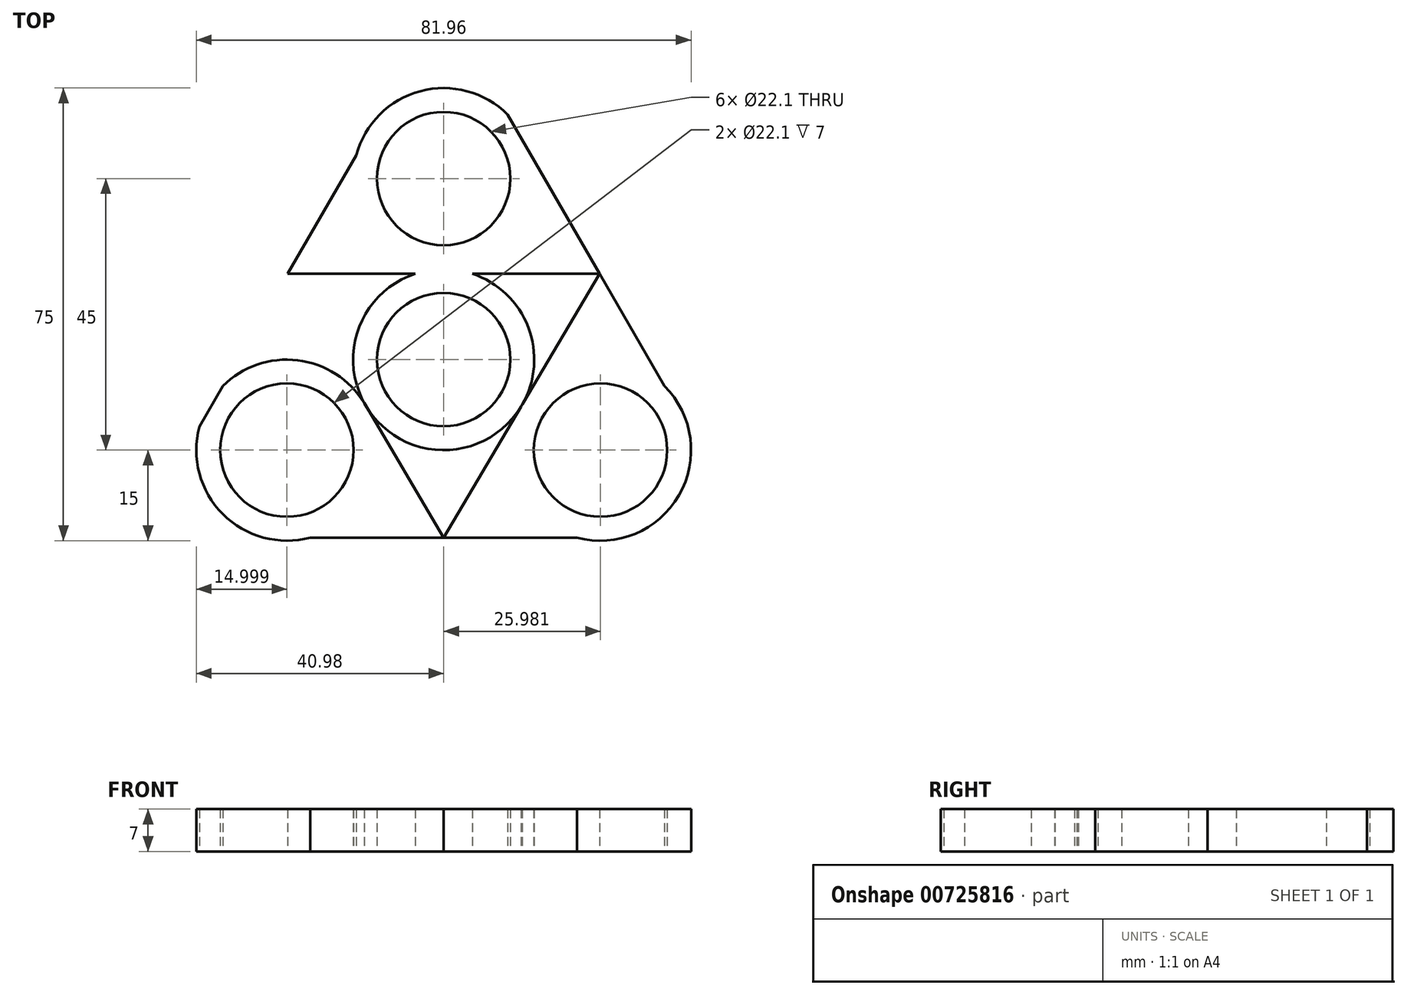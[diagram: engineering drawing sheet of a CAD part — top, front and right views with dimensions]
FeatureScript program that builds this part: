
annotation { "Feature Type Name" : "Feature", "Feature Type Description" : "" }
export const myFeature = defineFeature(function(context is Context, id is Id, definition is map)
    precondition{}
    {
        {
            var Q0;
            Q0=qCreatedBy(makeId("Top.planeOp"),FACE);
            var sketch = newSketch(context, id + "F0", { "sketchPlane" : qUnion([Q0])});
            skCircle(sketch, "E0", {"center": v(0, 0) * mm, "radius": 11.05 * mm});
            skCircle(sketch, "E1", {"center": v(0, 0) * mm, "radius": 15 * mm});
            skCircle(sketch, "E2", {"center": v(0, 30) * mm, "radius": 11.05 * mm});
            skCircle(sketch, "E3", {"center": v(0, 30) * mm, "radius": 15 * mm});
            skCircle(sketch, "E4", {"center": v(-25.98, -15) * mm, "radius": 11.05 * mm});
            skCircle(sketch, "E5", {"center": v(25.98, -15) * mm, "radius": 11.05 * mm});
            skCircle(sketch, "E6", {"center": v(-25.98, -15) * mm, "radius": 15 * mm});
            skCircle(sketch, "E7", {"center": v(25.98, -15) * mm, "radius": 15 * mm});
            skLineSegment(sketch, "E8", {"start": v(0, 30) * mm, "end": v(0, 0) * mm, "construction": true});
            skLineSegment(sketch, "E9", {"start": v(-25.98, -15) * mm, "end": v(0, 0) * mm, "construction": true});
            skLineSegment(sketch, "E10", {"start": v(25.98, -15) * mm, "end": v(0, 0) * mm, "construction": true});
            skLineSegment(sketch, "E11", {"start": v(-25.98, -15) * mm, "end": v(-33.48, -2) * mm, "construction": true});
            skLineSegment(sketch, "E12", {"start": v(0, 30) * mm, "end": v(-15, 30) * mm, "construction": true});
            skLineSegment(sketch, "E13", {"start": v(0, 30) * mm, "end": v(15, 30) * mm, "construction": true});
            skLineSegment(sketch, "E14", {"start": v(25.98, -15) * mm, "end": v(33.48, -2) * mm, "construction": true});
            skLineSegment(sketch, "E15", {"start": v(33.48, -2) * mm, "end": v(18.48, -28) * mm, "construction": true});
            skLineSegment(sketch, "E16", {"start": v(0, 30) * mm, "end": v(-10.6, 40.6) * mm, "construction": true});
            skLineSegment(sketch, "E17", {"start": v(0, 30) * mm, "end": v(10.6, 40.6) * mm, "construction": true});
            skLineSegment(sketch, "E18", {"start": v(-25.98, -15) * mm, "end": v(-40.47, -11.12) * mm, "construction": true});
            skLineSegment(sketch, "E19", {"start": v(-25.98, -15) * mm, "end": v(-18.48, -28) * mm, "construction": true});
            skLineSegment(sketch, "E20", {"start": v(-25.98, -15) * mm, "end": v(-29.86, -29.49) * mm, "construction": true});
            skLineSegment(sketch, "E21", {"start": v(25.98, -15) * mm, "end": v(29.86, -29.49) * mm, "construction": true});
            skLineSegment(sketch, "E22", {"start": v(25.98, -15) * mm, "end": v(40.47, -11.12) * mm, "construction": true});
            skLineSegment(sketch, "E23", {"start": v(-40.47, -11.12) * mm, "end": v(-10.6, 40.6) * mm});
            skLineSegment(sketch, "E24", {"start": v(-29.86, -29.49) * mm, "end": v(29.86, -29.49) * mm});
            skLineSegment(sketch, "E25", {"start": v(10.6, 40.6) * mm, "end": v(40.47, -11.12) * mm});
            skLineSegment(sketch, "E26", {"start": v(-25.83, 14.24) * mm, "end": v(0, -29.49) * mm});
            skLineSegment(sketch, "E27", {"start": v(0, -29.49) * mm, "end": v(25.83, 14.24) * mm});
            skLineSegment(sketch, "E28", {"start": v(-25.83, 14.24) * mm, "end": v(25.83, 14.24) * mm, "construction": true});
            skLineSegment(sketch, "E29", {"start": v(-25.83, 14.24) * mm, "end": v(25.83, 14.24) * mm});
            skSolve(sketch);
        }
        {
            var Q0;
            {var subQ0=sQuery(id+"F0.wireOp",EDGE,"E25");var subQ1=sQuery(id+"F0.wireOp",EDGE,"E3");var subQ2=makeQuery(id+"F0.imprint","INTERSECT",VERTEX,{"disambiguationData":[OD(0.0)],"derivedFrom":[subQ1,subQ0]});Q0=makeQuery(id+"F0.imprint","IMPRINT",FACE,{"disambiguationData":[TD([[makeQuery(id+"F0.imprint","IMPRINT",EDGE,{"disambiguationData":[TD([[subQ2,1.0]])],"derivedFrom":subQ1}),1.0]])]});}
            var Q1;
            {var subQ0=sQuery(id+"F0.wireOp",EDGE,"E23");var subQ1=sQuery(id+"F0.wireOp",EDGE,"E3");var subQ2=makeQuery(id+"F0.imprint","INTERSECT",VERTEX,{"disambiguationData":[OD(0.0)],"derivedFrom":[subQ1,subQ0]});Q1=makeQuery(id+"F0.imprint","IMPRINT",FACE,{"disambiguationData":[TD([[makeQuery(id+"F0.imprint","IMPRINT",EDGE,{"disambiguationData":[TD([[subQ2,-1.0]])],"derivedFrom":subQ1}),1.0]])]});}
            var Q2;
            {var subQ0=sQuery(id+"F0.wireOp",EDGE,"E23");var subQ1=sQuery(id+"F0.wireOp",EDGE,"E6");var subQ2=makeQuery(id+"F0.imprint","INTERSECT",VERTEX,{"disambiguationData":[OD(0.0)],"derivedFrom":[subQ1,subQ0]});Q2=makeQuery(id+"F0.imprint","IMPRINT",FACE,{"disambiguationData":[TD([[makeQuery(id+"F0.imprint","IMPRINT",EDGE,{"disambiguationData":[TD([[subQ2,1.0]])],"derivedFrom":subQ1}),1.0]])]});}
            var Q3;
            {var subQ0=sQuery(id+"F0.wireOp",EDGE,"E24");var subQ1=sQuery(id+"F0.wireOp",EDGE,"E6");var subQ2=makeQuery(id+"F0.imprint","INTERSECT",VERTEX,{"disambiguationData":[OD(0.0)],"derivedFrom":[subQ1,subQ0]});Q3=makeQuery(id+"F0.imprint","IMPRINT",FACE,{"disambiguationData":[TD([[makeQuery(id+"F0.imprint","IMPRINT",EDGE,{"disambiguationData":[TD([[subQ2,-1.0]])],"derivedFrom":subQ1}),1.0]])]});}
            var Q4;
            {var subQ0=sQuery(id+"F0.wireOp",EDGE,"E25");var subQ1=sQuery(id+"F0.wireOp",EDGE,"E7");var subQ2=makeQuery(id+"F0.imprint","INTERSECT",VERTEX,{"disambiguationData":[OD(0.0)],"derivedFrom":[subQ1,subQ0]});Q4=makeQuery(id+"F0.imprint","IMPRINT",FACE,{"disambiguationData":[TD([[makeQuery(id+"F0.imprint","IMPRINT",EDGE,{"disambiguationData":[TD([[subQ2,-1.0]])],"derivedFrom":subQ1}),1.0]])]});}
            var Q5;
            {var subQ0=sQuery(id+"F0.wireOp",EDGE,"E24");var subQ1=sQuery(id+"F0.wireOp",EDGE,"E7");var subQ2=makeQuery(id+"F0.imprint","INTERSECT",VERTEX,{"disambiguationData":[OD(0.0)],"derivedFrom":[subQ1,subQ0]});Q5=makeQuery(id+"F0.imprint","IMPRINT",FACE,{"disambiguationData":[TD([[makeQuery(id+"F0.imprint","IMPRINT",EDGE,{"disambiguationData":[TD([[subQ2,1.0]])],"derivedFrom":subQ1}),1.0]])]});}
            var Q6;
            {var subQ0=sQuery(id+"F0.wireOp",EDGE,"E23");var subQ1=sQuery(id+"F0.wireOp",EDGE,"E6");var subQ2=makeQuery(id+"F0.imprint","INTERSECT",VERTEX,{"disambiguationData":[OD(1.0)],"derivedFrom":[subQ1,subQ0]});Q6=makeQuery(id+"F0.imprint","IMPRINT",FACE,{"disambiguationData":[TD([[makeQuery(id+"F0.imprint","IMPRINT",EDGE,{"disambiguationData":[TD([[subQ2,1.0]])],"derivedFrom":subQ1}),-1.0]])]});}
            var Q7;
            {var subQ0=sQuery(id+"F0.wireOp",EDGE,"E25");var subQ1=sQuery(id+"F0.wireOp",EDGE,"E7");var subQ2=makeQuery(id+"F0.imprint","INTERSECT",VERTEX,{"disambiguationData":[OD(1.0)],"derivedFrom":[subQ1,subQ0]});Q7=makeQuery(id+"F0.imprint","IMPRINT",FACE,{"disambiguationData":[TD([[makeQuery(id+"F0.imprint","IMPRINT",EDGE,{"disambiguationData":[TD([[subQ2,-1.0]])],"derivedFrom":subQ1}),-1.0]])]});}
            var Q8;
            {var subQ0=sQuery(id+"F0.wireOp",EDGE,"E3");var subQ1=sQuery(id+"F0.wireOp",EDGE,"E1");var subQ2=makeQuery(id+"F0.imprint","INTERSECT",VERTEX,{"derivedFrom":[subQ1,subQ0]});Q8=makeQuery(id+"F0.imprint","IMPRINT",FACE,{"disambiguationData":[TD([[makeQuery(id+"F0.imprint","IMPRINT",EDGE,{"disambiguationData":[TD([[subQ2,1.0]])],"derivedFrom":subQ1}),-1.0]])]});}
            var Q9;
            {var subQ0=sQuery(id+"F0.wireOp",EDGE,"E3");var subQ1=sQuery(id+"F0.wireOp",EDGE,"E1");var subQ2=makeQuery(id+"F0.imprint","INTERSECT",VERTEX,{"derivedFrom":[subQ1,subQ0]});Q9=makeQuery(id+"F0.imprint","IMPRINT",FACE,{"disambiguationData":[TD([[makeQuery(id+"F0.imprint","IMPRINT",EDGE,{"disambiguationData":[TD([[subQ2,-1.0]])],"derivedFrom":subQ1}),-1.0]])]});}
            var Q10;
            {var subQ0=sQuery(id+"F0.wireOp",EDGE,"E27");var subQ1=sQuery(id+"F0.wireOp",EDGE,"E1");var subQ2=makeQuery(id+"F0.imprint","INTERSECT",VERTEX,{"disambiguationData":[OD(0.0)],"derivedFrom":[subQ1,subQ0]});Q10=makeQuery(id+"F0.imprint","IMPRINT",FACE,{"disambiguationData":[TD([[makeQuery(id+"F0.imprint","IMPRINT",EDGE,{"disambiguationData":[TD([[subQ2,-1.0]])],"derivedFrom":subQ1}),-1.0]])]});}
            var Q11;
            {var subQ0=sQuery(id+"F0.wireOp",EDGE,"E24");var subQ1=sQuery(id+"F0.wireOp",EDGE,"E6");var subQ2=makeQuery(id+"F0.imprint","INTERSECT",VERTEX,{"disambiguationData":[OD(1.0)],"derivedFrom":[subQ1,subQ0]});Q11=makeQuery(id+"F0.imprint","IMPRINT",FACE,{"disambiguationData":[TD([[makeQuery(id+"F0.imprint","IMPRINT",EDGE,{"disambiguationData":[TD([[subQ2,-1.0]])],"derivedFrom":subQ1}),-1.0]])]});}
            var Q12;
            Q12=makeQuery(id+"F0.imprint","IMPRINT",FACE,{"disambiguationData":[TD([[makeQuery(id+"F0.imprint","IMPRINT",EDGE,{"derivedFrom":sQuery(id+"F0.wireOp",EDGE,"E2")}),-1.0]])]});
            var Q13;
            Q13=makeQuery(id+"F0.imprint","IMPRINT",FACE,{"disambiguationData":[TD([[makeQuery(id+"F0.imprint","IMPRINT",EDGE,{"derivedFrom":sQuery(id+"F0.wireOp",EDGE,"E4")}),-1.0]])]});
            var Q14;
            Q14=makeQuery(id+"F0.imprint","IMPRINT",FACE,{"disambiguationData":[TD([[makeQuery(id+"F0.imprint","IMPRINT",EDGE,{"derivedFrom":sQuery(id+"F0.wireOp",EDGE,"E5")}),-1.0]])]});
            var Q15;
            Q15=makeQuery(id+"F0.imprint","IMPRINT",FACE,{"disambiguationData":[TD([[makeQuery(id+"F0.imprint","IMPRINT",EDGE,{"derivedFrom":sQuery(id+"F0.wireOp",EDGE,"E0")}),-1.0]])]});
            var Q16;
            {var subQ0=sQuery(id+"F0.wireOp",EDGE,"E1");var subQ1=makeQuery(id+"F0.imprint","INTERSECT",VERTEX,{"derivedFrom":[subQ0,sQuery(id+"F0.wireOp",EDGE,"E3")]});Q16=makeQuery(id+"F0.imprint","IMPRINT",FACE,{"disambiguationData":[TD([[makeQuery(id+"F0.imprint","IMPRINT",EDGE,{"disambiguationData":[TD([[subQ1,1.0]])],"derivedFrom":subQ0}),1.0]])]});}
            extrude(context, id + "F1", {"entities" : qUnion([Q0, Q1, Q2, Q3, Q4, Q5, Q6, Q7, Q8, Q9, Q10, Q11, Q12, Q13, Q14, Q15, Q16]), "depth" : 7 * mm, "offsetDistance" : 25 * mm});
        }
    });
